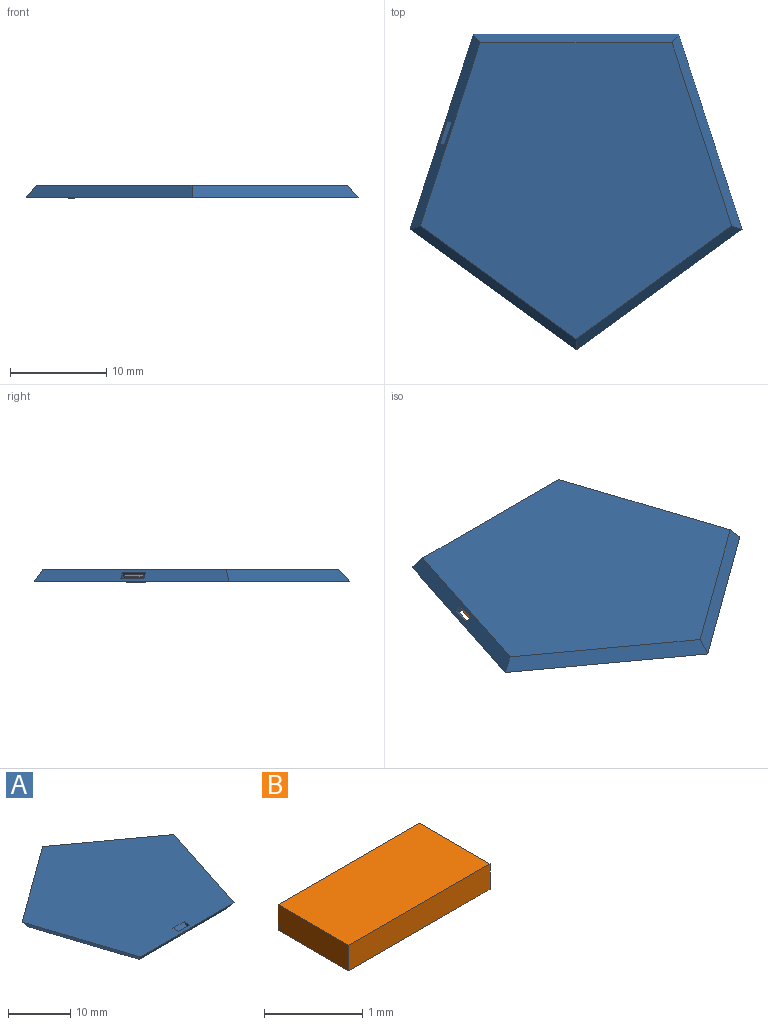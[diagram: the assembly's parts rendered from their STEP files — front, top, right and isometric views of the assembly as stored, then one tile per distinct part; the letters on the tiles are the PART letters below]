
ASSEMBLY  parts=2 mates=1
PART A: 11 faces, bbox 34.5x32.8x1.3 mm
  f0: plane 21.34x1.27mm, normal (0,-0.81,-0.59), area 30.5mm2, adj f1,f4,f5,f6,f7,f8,f9,f10
  f1: plane 34.53x32.84mm, normal (0,0,1), area 780.3mm2, adj f0,f2,f3,f4,f5,f7,f8,f9
  f2: plane 17.27x12.9mm, normal (0.48,0.65,-0.59), area 32.4mm2, adj f1,f3,f5,f6
  f3: plane 17.27x12.9mm, normal (-0.48,0.65,-0.59), area 32.4mm2, adj f1,f2,f4,f6
  f4: plane 20.3x7.27mm, normal (-0.77,-0.25,-0.59), area 32.4mm2, adj f0,f1,f3,f6
  f5: plane 20.3x7.27mm, normal (0.77,-0.25,-0.59), area 32.4mm2, adj f0,f1,f2,f6
  f6: plane 32.36x30.78mm, normal (0,0,-1), area 688.2mm2, adj f0,f2,f3,f4,f5
  f7: plane 2.54x1.28mm, normal (0,-0.59,0.81), area 4mm2, adj f0,f1,f8,f10
  f8: plane 1.73x0.93mm, normal (-1,0,0), area 0.8mm2, adj f0,f1,f7,f9
  f9: plane 2.54x0.43mm, normal (0,0.59,-0.81), area 1.4mm2, adj f0,f1,f8,f10
  f10: plane 1.73x0.93mm, normal (1,0,0), area 0.8mm2, adj f0,f1,f7,f9
PART B: 6 faces, bbox 2x1x0.3 mm
  f0: plane 2.03x0.32mm, normal (0,-1,0), area 0.6mm2, adj f1,f3,f4,f5
  f1: plane 1.02x0.32mm, normal (1,0,0), area 0.3mm2, adj f0,f2,f4,f5
  f2: plane 2.03x0.32mm, normal (0,1,0), area 0.6mm2, adj f1,f3,f4,f5
  f3: plane 1.02x0.32mm, normal (-1,0,0), area 0.3mm2, adj f0,f2,f4,f5
  f4: plane 2.03x1.02mm, normal (0,0,1), area 2.1mm2, adj f0,f1,f2,f3
  f5: plane 2.03x1.02mm, normal (0,0,-1), area 2.1mm2, adj f0,f1,f2,f3
PLACE A rot(axis=(0.81,0.59,0),180deg) t=(6.21,-8.33,-5.81)mm
PLACE B rot(axis=(-0.22,0.3,-0.93),112deg) t=(-6.68,-4.14,-6.87)mm
MATE fastened B.f4 <-> A.f7  axis (0.56,-0.18,0.81) through (-6.5,-4.2,-6.62)mm
